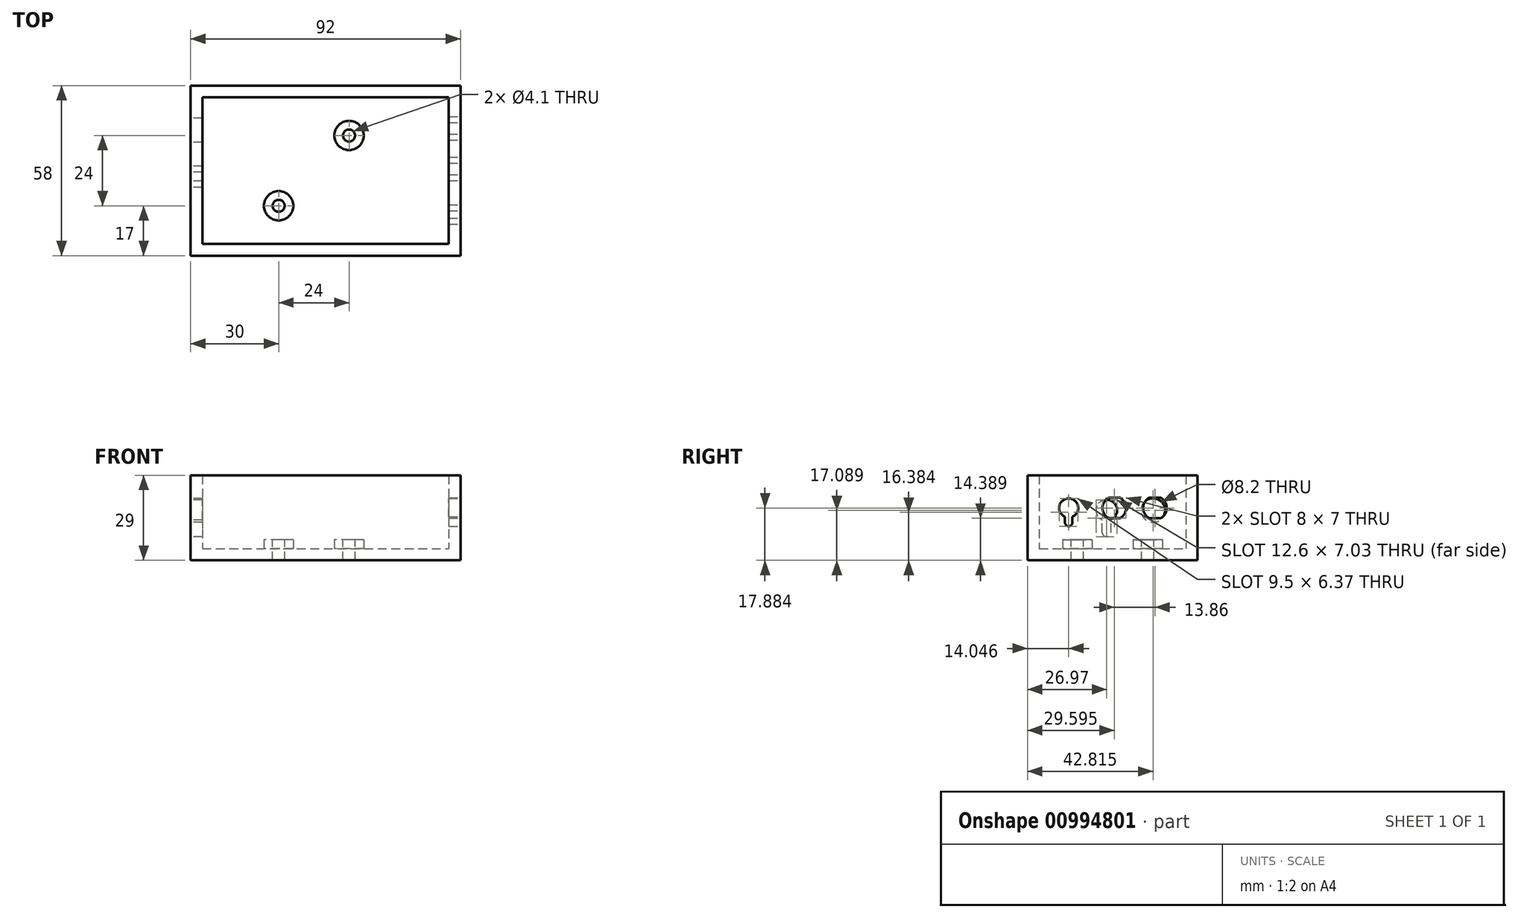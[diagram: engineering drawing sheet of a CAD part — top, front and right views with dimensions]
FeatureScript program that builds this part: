
annotation { "Feature Type Name" : "Feature", "Feature Type Description" : "" }
export const myFeature = defineFeature(function(context is Context, id is Id, definition is map)
    precondition{}
    {
        {
            var Q0;
            Q0=qCreatedBy(makeId("Top.planeOp"),FACE);
            var sketch = newSketch(context, id + "F0", { "sketchPlane" : qUnion([Q0])});
            skLineSegment(sketch, "E0.bottom", {"start": v(0, 0) * mm, "end": v(44, 0) * mm, "construction": true});
            skLineSegment(sketch, "E0.top", {"start": v(0, -30) * mm, "end": v(44, -30) * mm, "construction": true});
            skLineSegment(sketch, "E0.left", {"start": v(0, 0) * mm, "end": v(0, -30) * mm, "construction": true});
            skLineSegment(sketch, "E0.right", {"start": v(44, 0) * mm, "end": v(44, -30) * mm, "construction": true});
            skPoint(sketch, "E1", {"position": v(35, -3) * mm});
            skPoint(sketch, "E2", {"position": v(11, -27) * mm});
            skCircle(sketch, "E3", {"center": v(35, -3) * mm, "radius": 5 * mm});
            skCircle(sketch, "E4", {"center": v(11, -27) * mm, "radius": 5 * mm});
            skLineSegment(sketch, "E5", {"start": v(-15, 10) * mm, "end": v(69, 10) * mm});
            skLineSegment(sketch, "E6", {"start": v(69, 10) * mm, "end": v(69, -40) * mm});
            skLineSegment(sketch, "E7", {"start": v(69, -40) * mm, "end": v(-15, -40) * mm});
            skLineSegment(sketch, "E8", {"start": v(-15, -40) * mm, "end": v(-15, 10) * mm});
            skLineSegment(sketch, "E9.0", {"start": v(-19, 14) * mm, "end": v(73, 14) * mm});
            skLineSegment(sketch, "E9.1", {"start": v(-19, -44) * mm, "end": v(-19, 14) * mm});
            skLineSegment(sketch, "E9.2", {"start": v(73, -44) * mm, "end": v(-19, -44) * mm});
            skLineSegment(sketch, "E9.3", {"start": v(73, 14) * mm, "end": v(73, -44) * mm});
            skSolve(sketch);
        }
        {
            var Q0;
            Q0 = qSketchRegion(id + "F0", true);
            var Q1;
            Q1=makeQuery(id+"F0.imprint","IMPRINT",FACE,{"disambiguationData":[TD([[makeQuery(id+"F0.imprint","IMPRINT",EDGE,{"derivedFrom":sQuery(id+"F0.wireOp",EDGE,"E3")}),-1.0]])]});
            var Q2;
            Q2=makeQuery(id+"F0.imprint","IMPRINT",FACE,{"disambiguationData":[TD([[makeQuery(id+"F0.imprint","IMPRINT",EDGE,{"derivedFrom":sQuery(id+"F0.wireOp",EDGE,"E4")}),1.0]])]});
            var Q3;
            Q3=makeQuery(id+"F0.imprint","IMPRINT",FACE,{"disambiguationData":[TD([[makeQuery(id+"F0.imprint","IMPRINT",EDGE,{"derivedFrom":sQuery(id+"F0.wireOp",EDGE,"E3")}),1.0]])]});
            extrude(context, id + "F1", {"entities" : qUnion([Q0, Q1, Q2, Q3]), "oppositeDirection" : true, "depth" : 4 * mm, "offsetDistance" : 25 * mm});
        }
        {
            var Q0;
            Q0 = qSketchRegion(id + "F0", true);
            extrude(context, id + "F2", {"entities" : qUnion([Q0]), "operationType" : NewBodyOperationType.ADD, "depth" : 25 * mm, "offsetDistance" : 25 * mm});
        }
        {
            var Q0;
            Q0=makeQuery(id+"F0.imprint","IMPRINT",FACE,{"disambiguationData":[TD([[makeQuery(id+"F0.imprint","IMPRINT",EDGE,{"derivedFrom":sQuery(id+"F0.wireOp",EDGE,"E3")}),1.0]])]});
            var Q1;
            Q1=makeQuery(id+"F0.imprint","IMPRINT",FACE,{"disambiguationData":[TD([[makeQuery(id+"F0.imprint","IMPRINT",EDGE,{"derivedFrom":sQuery(id+"F0.wireOp",EDGE,"E4")}),1.0]])]});
            extrude(context, id + "F3", {"entities" : qUnion([Q0, Q1]), "operationType" : NewBodyOperationType.ADD, "depth" : 3 * mm, "offsetDistance" : 25 * mm});
        }
        {
            var Q0;
            {var subQ0=sQuery(id+"F0.wireOp",EDGE,"E9.3");Q0=makeQuery(id+"F2.boolean.opBoolean","MERGE",FACE,{"derivedFrom":[makeQuery(id+"F1.opExtrude","SWEPT_FACE",FACE,{"disambiguationData":[OSD([subQ0])]}),makeQuery(id+"F2.opExtrude","SWEPT_FACE",FACE,{"disambiguationData":[OSD([subQ0])]})]});}
            var sketch = newSketch(context, id + "F4", { "sketchPlane" : qUnion([Q0])});
            skPoint(sketch, "E10", {"position": v(-14.4, 13.88) * mm});
            skPoint(sketch, "E11", {"position": v(-0.55, 13.88) * mm});
            skArc(sketch, "E12", {"start": v(-16.34, 17.38) * mm, "mid": v(-18.4, 13.88) * mm, "end": v(-16.34, 10.38) * mm});
            skArc(sketch, "E13", {"start": v(1.4, 10.38) * mm, "mid": v(3.45, 13.88) * mm, "end": v(1.4, 17.38) * mm});
            skPoint(sketch, "E14", {"position": v(-29.95, 13.88) * mm});
            skArc(sketch, "E15", {"start": v(-28.7, 10.88) * mm, "mid": v(-29.95, 17.13) * mm, "end": v(-31.2, 10.88) * mm});
            skPoint(sketch, "E16", {"position": v(-29.95, 8.88) * mm});
            skArc(sketch, "E17", {"start": v(-31.2, 8.88) * mm, "mid": v(-29.95, 7.63) * mm, "end": v(-28.7, 8.88) * mm});
            skLineSegment(sketch, "E18", {"start": v(-31.2, 8.88) * mm, "end": v(-31.2, 10.88) * mm});
            skLineSegment(sketch, "E19", {"start": v(-28.7, 8.88) * mm, "end": v(-28.7, 10.88) * mm});
            skLineSegment(sketch, "E20", {"start": v(-16.34, 17.38) * mm, "end": v(-12.47, 17.38) * mm});
            skLineSegment(sketch, "E21", {"start": v(-16.34, 10.38) * mm, "end": v(-12.47, 10.38) * mm});
            skPoint(sketch, "E22", {"position": v(-12.47, 10.38) * mm});
            skPoint(sketch, "E23", {"position": v(-2.48, 10.38) * mm});
            skPoint(sketch, "E24", {"position": v(-12.47, 17.38) * mm});
            skPoint(sketch, "E25", {"position": v(-2.48, 17.38) * mm});
            skLineSegment(sketch, "E26.trimOffspring", {"start": v(-2.48, 17.38) * mm, "end": v(1.4, 17.38) * mm});
            skLineSegment(sketch, "E27.trimOffspring", {"start": v(-2.48, 10.38) * mm, "end": v(1.4, 10.38) * mm});
            skArc(sketch, "E28.trimOffspring", {"start": v(-12.47, 10.38) * mm, "mid": v(-10.4, 13.88) * mm, "end": v(-12.47, 17.38) * mm});
            skArc(sketch, "E29.trimOffspring", {"start": v(-2.48, 17.38) * mm, "mid": v(-4.55, 13.88) * mm, "end": v(-2.48, 10.38) * mm});
            skCircle(sketch, "E30", {"center": v(-14.4, 13.88) * mm, "radius": 6 * mm, "construction": true});
            skCircle(sketch, "E31", {"center": v(-0.55, 13.88) * mm, "radius": 6 * mm, "construction": true});
            skSolve(sketch);
        }
        {
            var Q0;
            Q0=makeQuery(id+"F4.imprint","IMPRINT",FACE,{"disambiguationData":[TD([[makeQuery(id+"F4.imprint","IMPRINT",EDGE,{"derivedFrom":sQuery(id+"F4.wireOp",EDGE,"E15")}),1.0]])]});
            var Q1;
            Q1=makeQuery(id+"F4.imprint","IMPRINT",FACE,{"disambiguationData":[TD([[makeQuery(id+"F4.imprint","IMPRINT",EDGE,{"derivedFrom":sQuery(id+"F4.wireOp",EDGE,"E12")}),1.0]])]});
            var Q2;
            Q2=makeQuery(id+"F4.imprint","IMPRINT",FACE,{"disambiguationData":[TD([[makeQuery(id+"F4.imprint","IMPRINT",EDGE,{"derivedFrom":sQuery(id+"F4.wireOp",EDGE,"E13")}),1.0]])]});
            extrude(context, id + "F5", {"entities" : qUnion([Q0, Q1, Q2]), "operationType" : NewBodyOperationType.REMOVE, "endBound" : BoundingType.UP_TO_NEXT, "oppositeDirection" : true, "depth" : 25 * mm, "offsetDistance" : 25 * mm});
        }
        {
            var Q0;
            {var subQ0=sQuery(id+"F0.wireOp",EDGE,"E9.1");Q0=makeQuery(id+"F2.boolean.opBoolean","MERGE",FACE,{"derivedFrom":[makeQuery(id+"F1.opExtrude","SWEPT_FACE",FACE,{"disambiguationData":[OSD([subQ0])]}),makeQuery(id+"F2.opExtrude","SWEPT_FACE",FACE,{"disambiguationData":[OSD([subQ0])]})]});}
            var sketch = newSketch(context, id + "F6", { "sketchPlane" : qUnion([Q0])});
            skCircle(sketch, "E32", {"center": v(1.19, 13.09) * mm, "radius": 4.1 * mm});
            skArc(sketch, "E33", {"start": v(18.53, 9.82) * mm, "mid": v(17.03, 16.69) * mm, "end": v(15.53, 9.82) * mm});
            skArc(sketch, "E34", {"start": v(15.53, 5.59) * mm, "mid": v(17.03, 4.09) * mm, "end": v(18.53, 5.59) * mm});
            skLineSegment(sketch, "E35", {"start": v(15.53, 5.59) * mm, "end": v(15.53, 9.82) * mm});
            skLineSegment(sketch, "E36", {"start": v(18.53, 5.59) * mm, "end": v(18.53, 9.82) * mm});
            skLineSegment(sketch, "E37", {"start": v(38.03, 22.53) * mm, "end": v(38.03, 2.36) * mm, "construction": true});
            skCircle(sketch, "E38", {"center": v(17.03, 13.09) * mm, "radius": 8.5 * mm, "construction": true});
            skCircle(sketch, "E39", {"center": v(1.19, 13.09) * mm, "radius": 6 * mm, "construction": true});
            skSolve(sketch);
        }
        {
            var Q0;
            Q0=makeQuery(id+"F6.imprint","IMPRINT",FACE,{"disambiguationData":[TD([[makeQuery(id+"F6.imprint","IMPRINT",EDGE,{"derivedFrom":sQuery(id+"F6.wireOp",EDGE,"E32")}),1.0]])]});
            var Q1;
            Q1=makeQuery(id+"F6.imprint","IMPRINT",FACE,{"disambiguationData":[TD([[makeQuery(id+"F6.imprint","IMPRINT",EDGE,{"derivedFrom":sQuery(id+"F6.wireOp",EDGE,"E33")}),1.0]])]});
            extrude(context, id + "F7", {"entities" : qUnion([Q0, Q1]), "operationType" : NewBodyOperationType.REMOVE, "endBound" : BoundingType.UP_TO_NEXT, "oppositeDirection" : true, "depth" : 25 * mm, "offsetDistance" : 25 * mm});
        }
        {
            var Q0;
            Q0=makeQuery(id+"F3.opExtrude","CAP_FACE",FACE,{"disambiguationData":[OSD([sQuery(id+"F0.wireOp",EDGE,"E4")])],"isStart":false});
            var sketch = newSketch(context, id + "F8", { "sketchPlane" : qUnion([Q0])});
            skPoint(sketch, "E40.0", {"position": v(11, -27) * mm});
            skPoint(sketch, "E41.0", {"position": v(35, -3) * mm});
            skSolve(sketch);
        }
        {
            var Q0;
            Q0=sQuery(id+"F8.wireOp",VERTEX,"E41.0");
            var Q1;
            Q1=sQuery(id+"F8.wireOp",VERTEX,"E40.0");
            var Q2;
            Q2=makeQuery(id+"F1.opExtrude","SWEPT_BODY",BODY,{"disambiguationData":[OSD([sQuery(id+"F0.wireOp",EDGE,"E9.0"),sQuery(id+"F0.wireOp",EDGE,"E9.1"),sQuery(id+"F0.wireOp",EDGE,"E9.2"),sQuery(id+"F0.wireOp",EDGE,"E9.3")])]});
            hole(context, id + "F9", {"style" : HoleStyle.SIMPLE, "endStyle" : HoleEndStyle.THROUGH, "holeDiameter" : 4.1 * mm, "majorDiameter" : 5 * mm, "tappedDepth" : 12 * mm, "tapClearance" : 3, "locations" : qUnion([Q0, Q1]), "scope" : qUnion([Q2])});
        }
    });
